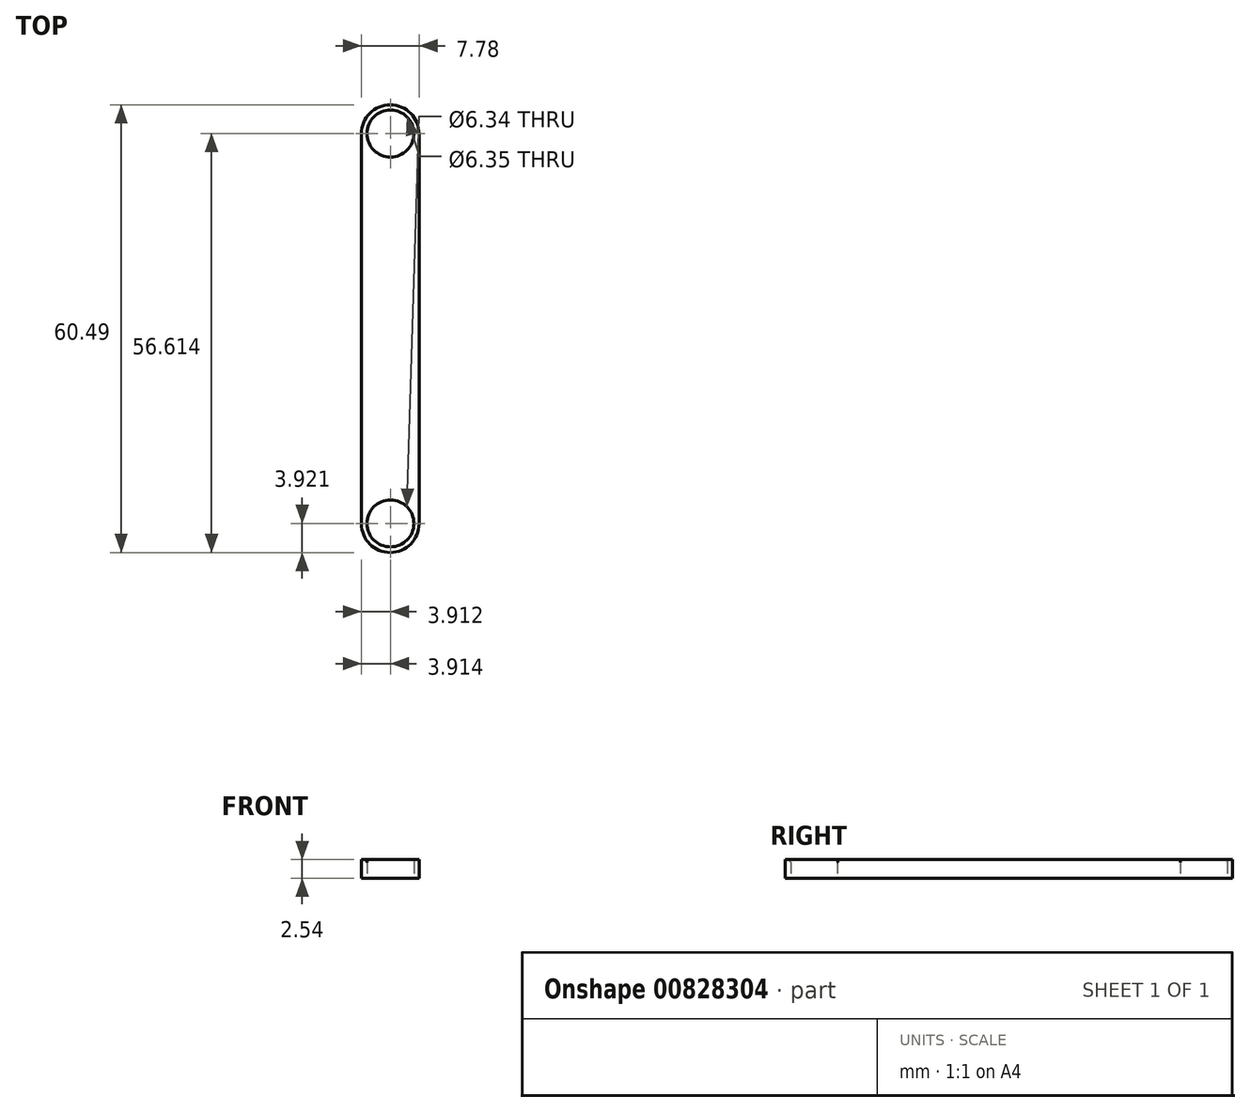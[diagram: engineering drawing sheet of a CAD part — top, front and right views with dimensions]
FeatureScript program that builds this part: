
annotation { "Feature Type Name" : "Feature", "Feature Type Description" : "" }
export const myFeature = defineFeature(function(context is Context, id is Id, definition is map)
    precondition{}
    {
        {
            var Q0;
            Q0=qCreatedBy(makeId("Top.planeOp"),FACE);
            var sketch = newSketch(context, id + "F0", { "sketchPlane" : qUnion([Q0])});
            skLineSegment(sketch, "E0", {"start": v(-39.53, 37.82) * mm, "end": v(-39.53, -14.88) * mm});
            skLineSegment(sketch, "E1", {"start": v(-31.75, -14.88) * mm, "end": v(-31.75, 37.82) * mm});
            skArc(sketch, "E2", {"start": v(-31.75, 37.82) * mm, "mid": v(-35.64, 41.72) * mm, "end": v(-39.53, 37.82) * mm});
            skArc(sketch, "E3", {"start": v(-39.53, -14.88) * mm, "mid": v(-35.64, -18.77) * mm, "end": v(-31.75, -14.88) * mm});
            skSolve(sketch);
        }
        {
            var Q0;
            Q0 = qSketchRegion(id + "F0", true);
            extrude(context, id + "F1", {"entities" : qUnion([Q0]), "depth" : 2.54 * mm, "offsetDistance" : 25.4 * mm});
        }
        {
            var Q0;
            Q0=qCreatedBy(makeId("Top.planeOp"),FACE);
            var sketch = newSketch(context, id + "F2", { "sketchPlane" : qUnion([Q0])});
            skCircle(sketch, "E4", {"center": v(-35.62, 37.84) * mm, "radius": 3.18 * mm});
            skCircle(sketch, "E5", {"center": v(-35.62, -14.85) * mm, "radius": 3.17 * mm});
            skSolve(sketch);
        }
        {
            var Q0;
            Q0 = qSketchRegion(id + "F2", true);
            extrude(context, id + "F3", {"entities" : qUnion([Q0]), "operationType" : NewBodyOperationType.REMOVE, "depth" : 3.8 * mm, "offsetDistance" : 25.4 * mm});
        }
        {
            var Q0;
            Q0=makeQuery(id+"F3.boolean.opBoolean","INTERSECT",EDGE,{"derivedFrom":[makeQuery(id+"F1.opExtrude","CAP_FACE",FACE,{"disambiguationData":[OSD([sQuery(id+"F0.wireOp",EDGE,"E0"),sQuery(id+"F0.wireOp",EDGE,"E1"),sQuery(id+"F0.wireOp",EDGE,"E2"),sQuery(id+"F0.wireOp",EDGE,"E3")])],"isStart":false}),makeQuery(id+"F3.opExtrude","SWEPT_FACE",FACE,{"disambiguationData":[OSD([sQuery(id+"F2.wireOp",EDGE,"E4")])]})]});
            var Q1;
            Q1=makeQuery(id+"F3.boolean.opBoolean","COPY",EDGE,{"derivedFrom":makeQuery(id+"F3.opExtrude","CAP_EDGE",EDGE,{"disambiguationData":[OSD([sQuery(id+"F2.wireOp",EDGE,"E4")])],"isStart":true})});
            var Q2;
            Q2=makeQuery(id+"F3.boolean.opBoolean","INTERSECT",EDGE,{"derivedFrom":[makeQuery(id+"F1.opExtrude","CAP_FACE",FACE,{"disambiguationData":[OSD([sQuery(id+"F0.wireOp",EDGE,"E0"),sQuery(id+"F0.wireOp",EDGE,"E1"),sQuery(id+"F0.wireOp",EDGE,"E2"),sQuery(id+"F0.wireOp",EDGE,"E3")])],"isStart":false}),makeQuery(id+"F3.opExtrude","SWEPT_FACE",FACE,{"disambiguationData":[OSD([sQuery(id+"F2.wireOp",EDGE,"E5")])]})]});
            var Q3;
            Q3=makeQuery(id+"F3.boolean.opBoolean","COPY",EDGE,{"derivedFrom":makeQuery(id+"F3.opExtrude","CAP_EDGE",EDGE,{"disambiguationData":[OSD([sQuery(id+"F2.wireOp",EDGE,"E5")])],"isStart":true})});
            fillet(context, id + "F4", {"entities" : qUnion([Q0, Q1, Q2, Q3]), "radius" : 0.38 * mm, "tangentPropagation" : true, "allowEdgeOverflow" : false});
        }
    });
